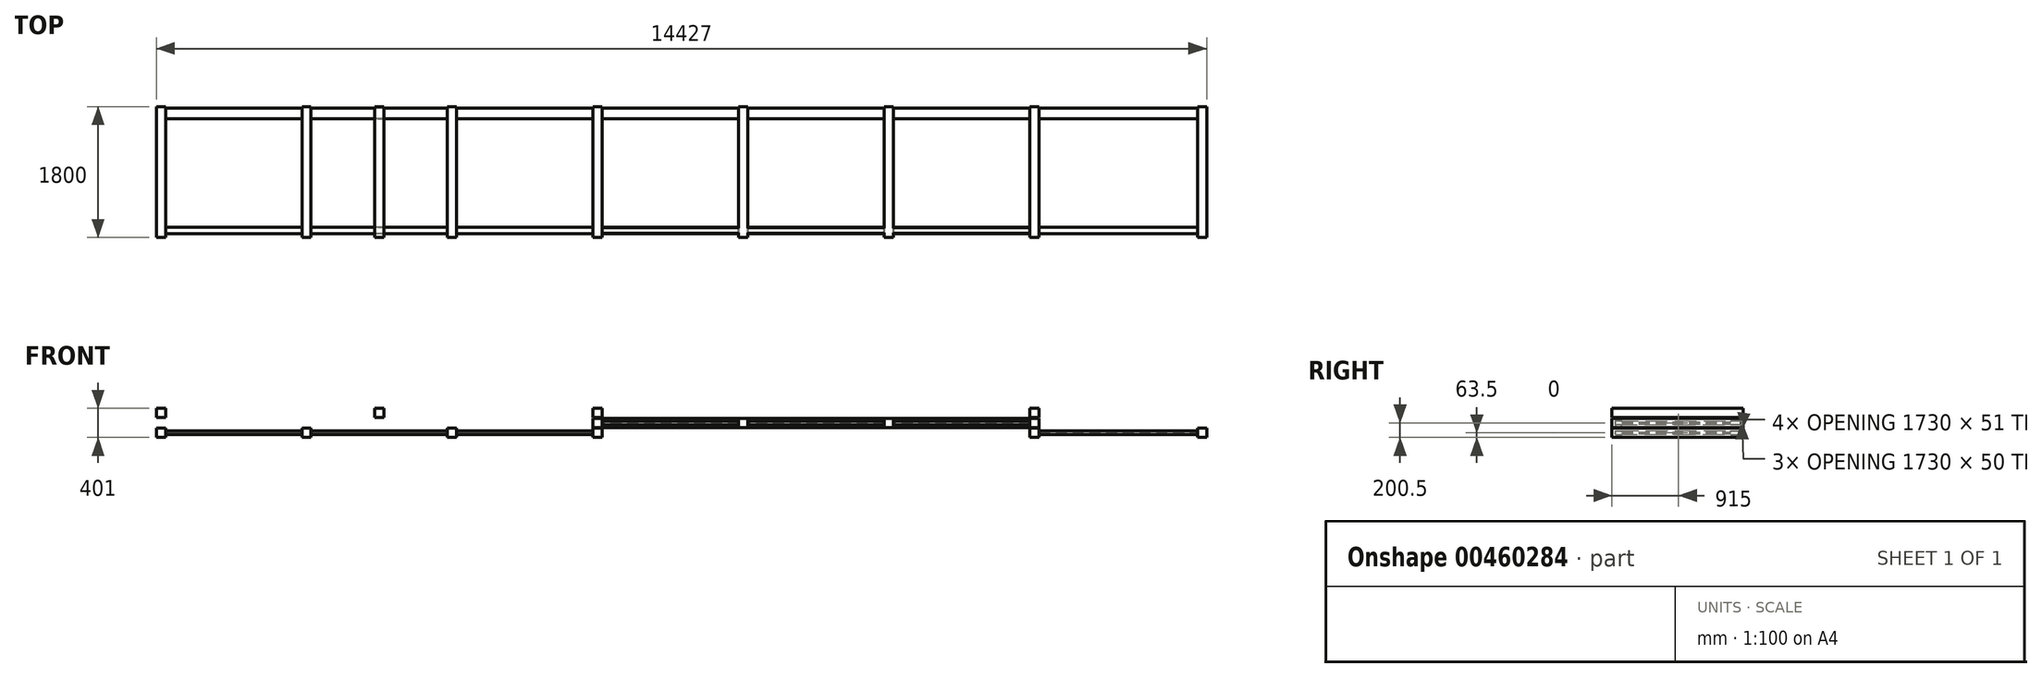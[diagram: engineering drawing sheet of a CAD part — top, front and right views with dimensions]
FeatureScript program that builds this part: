
annotation { "Feature Type Name" : "Feature", "Feature Type Description" : "" }
export const myFeature = defineFeature(function(context is Context, id is Id, definition is map)
    precondition{}
    {
        {
            var Q0;
            Q0=qCreatedBy(makeId("Front.planeOp"),FACE);
            var sketch = newSketch(context, id + "F0", { "sketchPlane" : qUnion([Q0])});
            skLineSegment(sketch, "E0.bottom", {"start": v(2923.43, -12.5) * mm, "end": v(-3076.57, -12.5) * mm});
            skLineSegment(sketch, "E0.top", {"start": v(2923.43, 12.5) * mm, "end": v(-3076.57, 12.5) * mm});
            skLineSegment(sketch, "E0.left", {"start": v(2923.43, -12.5) * mm, "end": v(2923.43, 12.5) * mm});
            skLineSegment(sketch, "E0.right", {"start": v(-3076.57, -12.5) * mm, "end": v(-3076.57, 12.5) * mm});
            skPoint(sketch, "E0.middle", {"position": v(-1076.57, 0) * mm});
            skLineSegment(sketch, "E1.bottom", {"start": v(2986.93, -63.5) * mm, "end": v(2859.93, -63.5) * mm});
            skLineSegment(sketch, "E1.top", {"start": v(2986.93, 63.5) * mm, "end": v(2859.93, 63.5) * mm});
            skLineSegment(sketch, "E1.left", {"start": v(2986.93, -63.5) * mm, "end": v(2986.93, 63.5) * mm});
            skLineSegment(sketch, "E1.right", {"start": v(2859.93, -63.5) * mm, "end": v(2859.93, 63.5) * mm});
            skPoint(sketch, "E1.middle", {"position": v(2923.43, 0) * mm});
            skLineSegment(sketch, "E2.bottom", {"start": v(-3013.07, -63.5) * mm, "end": v(-3140.07, -63.5) * mm});
            skLineSegment(sketch, "E2.top", {"start": v(-3013.07, 63.5) * mm, "end": v(-3140.07, 63.5) * mm});
            skLineSegment(sketch, "E2.left", {"start": v(-3013.07, -63.5) * mm, "end": v(-3013.07, 63.5) * mm});
            skLineSegment(sketch, "E2.right", {"start": v(-3140.07, -63.5) * mm, "end": v(-3140.07, 63.5) * mm});
            skPoint(sketch, "E2.middle", {"position": v(-3076.57, 0) * mm});
            skLineSegment(sketch, "E3.bottom", {"start": v(-1013.07, -63.5) * mm, "end": v(-1140.07, -63.5) * mm});
            skLineSegment(sketch, "E3.top", {"start": v(-1013.07, 63.5) * mm, "end": v(-1140.07, 63.5) * mm});
            skLineSegment(sketch, "E3.left", {"start": v(-1013.07, -63.5) * mm, "end": v(-1013.07, 63.5) * mm});
            skLineSegment(sketch, "E3.right", {"start": v(-1140.07, -63.5) * mm, "end": v(-1140.07, 63.5) * mm});
            skPoint(sketch, "E4.middle", {"position": v(923.43, 0) * mm});
            skLineSegment(sketch, "E5.bottom", {"start": v(986.93, -63.5) * mm, "end": v(859.93, -63.5) * mm});
            skLineSegment(sketch, "E5.top", {"start": v(986.93, 63.5) * mm, "end": v(859.93, 63.5) * mm});
            skLineSegment(sketch, "E5.left", {"start": v(986.93, -63.5) * mm, "end": v(986.93, 63.5) * mm});
            skLineSegment(sketch, "E5.right", {"start": v(859.93, -63.5) * mm, "end": v(859.93, 63.5) * mm});
            skLineSegment(sketch, "E6.bottom", {"start": v(-3013.07, -200.5) * mm, "end": v(-3140.07, -200.5) * mm});
            skLineSegment(sketch, "E6.top", {"start": v(-3013.07, -73.5) * mm, "end": v(-3140.07, -73.5) * mm});
            skLineSegment(sketch, "E6.left", {"start": v(-3013.07, -200.5) * mm, "end": v(-3013.07, -73.5) * mm});
            skLineSegment(sketch, "E6.right", {"start": v(-3140.07, -200.5) * mm, "end": v(-3140.07, -73.5) * mm});
            skPoint(sketch, "E6.middle", {"position": v(-3076.57, -137) * mm});
            skLineSegment(sketch, "E7.1.0.0", {"start": v(-5013.07, -200.5) * mm, "end": v(-5140.07, -200.5) * mm});
            skLineSegment(sketch, "E7.1.0.1", {"start": v(-5140.07, -200.5) * mm, "end": v(-5140.07, -73.5) * mm});
            skLineSegment(sketch, "E7.1.0.2", {"start": v(-5013.07, -73.5) * mm, "end": v(-5140.07, -73.5) * mm});
            skLineSegment(sketch, "E7.1.0.3", {"start": v(-5013.07, -200.5) * mm, "end": v(-5013.07, -73.5) * mm});
            skLineSegment(sketch, "E7.2.0.0", {"start": v(-7013.07, -200.5) * mm, "end": v(-7140.07, -200.5) * mm});
            skLineSegment(sketch, "E7.2.0.1", {"start": v(-7140.07, -200.5) * mm, "end": v(-7140.07, -73.5) * mm});
            skLineSegment(sketch, "E7.2.0.2", {"start": v(-7013.07, -73.5) * mm, "end": v(-7140.07, -73.5) * mm});
            skLineSegment(sketch, "E7.2.0.3", {"start": v(-7013.07, -200.5) * mm, "end": v(-7013.07, -73.5) * mm});
            skLineSegment(sketch, "E7.3.0.0", {"start": v(-9013.07, -200.5) * mm, "end": v(-9140.07, -200.5) * mm});
            skLineSegment(sketch, "E7.3.0.1", {"start": v(-9140.07, -200.5) * mm, "end": v(-9140.07, -73.5) * mm});
            skLineSegment(sketch, "E7.3.0.2", {"start": v(-9013.07, -73.5) * mm, "end": v(-9140.07, -73.5) * mm});
            skLineSegment(sketch, "E7.3.0.3", {"start": v(-9013.07, -200.5) * mm, "end": v(-9013.07, -73.5) * mm});
            skLineSegment(sketch, "E7.direction1", {"start": v(-3140.07, -200.5) * mm, "end": v(-5140.07, -200.5) * mm, "construction": true});
            skLineSegment(sketch, "E8", {"start": v(-9013.07, -126) * mm, "end": v(-3140.07, -126) * mm});
            skLineSegment(sketch, "E9", {"start": v(-3140.07, -148) * mm, "end": v(-9013.07, -148) * mm});
            skLineSegment(sketch, "E10.bottom", {"start": v(2986.93, -200.5) * mm, "end": v(2859.93, -200.5) * mm});
            skLineSegment(sketch, "E10.top", {"start": v(2986.93, -73.5) * mm, "end": v(2859.93, -73.5) * mm});
            skLineSegment(sketch, "E10.left", {"start": v(2986.93, -200.5) * mm, "end": v(2986.93, -73.5) * mm});
            skLineSegment(sketch, "E10.right", {"start": v(2859.93, -200.5) * mm, "end": v(2859.93, -73.5) * mm});
            skPoint(sketch, "E10.middle", {"position": v(2923.43, -137) * mm});
            skPoint(sketch, "E10.cornerSnap0", {"position": v(2986.93, 0) * mm});
            skLineSegment(sketch, "E11.1.0.0", {"start": v(5286.93, -200.5) * mm, "end": v(5159.93, -200.5) * mm});
            skLineSegment(sketch, "E11.1.0.1", {"start": v(5159.93, -200.5) * mm, "end": v(5159.93, -73.5) * mm});
            skLineSegment(sketch, "E11.1.0.2", {"start": v(5286.93, -73.5) * mm, "end": v(5159.93, -73.5) * mm});
            skLineSegment(sketch, "E11.1.0.3", {"start": v(5286.93, -200.5) * mm, "end": v(5286.93, -73.5) * mm});
            skLineSegment(sketch, "E11.direction1", {"start": v(2859.93, -200.5) * mm, "end": v(5159.93, -200.5) * mm, "construction": true});
            skLineSegment(sketch, "E12", {"start": v(2986.93, -126) * mm, "end": v(5159.93, -126) * mm});
            skLineSegment(sketch, "E13", {"start": v(2986.93, -148) * mm, "end": v(5159.93, -148) * mm});
            skLineSegment(sketch, "E14.bottom", {"start": v(2986.93, 73.5) * mm, "end": v(2859.93, 73.5) * mm});
            skLineSegment(sketch, "E14.top", {"start": v(2986.93, 200.5) * mm, "end": v(2859.93, 200.5) * mm});
            skLineSegment(sketch, "E14.left", {"start": v(2986.93, 73.5) * mm, "end": v(2986.93, 200.5) * mm});
            skLineSegment(sketch, "E14.right", {"start": v(2859.93, 73.5) * mm, "end": v(2859.93, 200.5) * mm});
            skPoint(sketch, "E14.middle", {"position": v(2923.43, 137) * mm});
            skLineSegment(sketch, "E15.bottom", {"start": v(-3013.07, 73.5) * mm, "end": v(-3140.07, 73.5) * mm});
            skLineSegment(sketch, "E15.top", {"start": v(-3013.07, 200.5) * mm, "end": v(-3140.07, 200.5) * mm});
            skLineSegment(sketch, "E15.left", {"start": v(-3013.07, 73.5) * mm, "end": v(-3013.07, 200.5) * mm});
            skLineSegment(sketch, "E15.right", {"start": v(-3140.07, 73.5) * mm, "end": v(-3140.07, 200.5) * mm});
            skPoint(sketch, "E15.middle", {"position": v(-3076.57, 137) * mm});
            skLineSegment(sketch, "E16.bottom", {"start": v(-9140.07, 73.5) * mm, "end": v(-9013.07, 73.5) * mm});
            skLineSegment(sketch, "E16.top", {"start": v(-9140.07, 200.5) * mm, "end": v(-9013.07, 200.5) * mm});
            skLineSegment(sketch, "E16.left", {"start": v(-9140.07, 73.5) * mm, "end": v(-9140.07, 200.5) * mm});
            skLineSegment(sketch, "E16.right", {"start": v(-9013.07, 73.5) * mm, "end": v(-9013.07, 200.5) * mm});
            skLineSegment(sketch, "E17.bottom", {"start": v(-6140.07, 73.5) * mm, "end": v(-6013.07, 73.5) * mm});
            skLineSegment(sketch, "E17.top", {"start": v(-6140.07, 200.5) * mm, "end": v(-6013.07, 200.5) * mm});
            skLineSegment(sketch, "E17.left", {"start": v(-6140.07, 73.5) * mm, "end": v(-6140.07, 200.5) * mm});
            skLineSegment(sketch, "E17.right", {"start": v(-6013.07, 73.5) * mm, "end": v(-6013.07, 200.5) * mm});
            skSolve(sketch);
        }
        {
            var Q0;
            {var subQ0=sQuery(id+"F0.wireOp",EDGE,"E3.right");var subQ1=sQuery(id+"F0.wireOp",EDGE,"E0.bottom");var subQ2=makeQuery(id+"F0.imprint","INTERSECT",VERTEX,{"derivedFrom":[subQ1,subQ0]});Q0=makeQuery(id+"F0.imprint","IMPRINT",FACE,{"disambiguationData":[TD([[makeQuery(id+"F0.imprint","IMPRINT",EDGE,{"disambiguationData":[TD([[subQ2,-1.0]])],"derivedFrom":subQ1}),-1.0]])]});}
            var Q1;
            {var subQ0=sQuery(id+"F0.wireOp",EDGE,"E0.right");Q1=makeQuery(id+"F0.imprint","IMPRINT",FACE,{"disambiguationData":[TD([[makeQuery(id+"F0.imprint","IMPRINT",EDGE,{"derivedFrom":subQ0}),-1.0]])]});}
            var Q2;
            {var subQ0=sQuery(id+"F0.wireOp",EDGE,"E3.left");var subQ1=sQuery(id+"F0.wireOp",EDGE,"E0.bottom");var subQ2=makeQuery(id+"F0.imprint","INTERSECT",VERTEX,{"derivedFrom":[subQ1,subQ0]});Q2=makeQuery(id+"F0.imprint","IMPRINT",FACE,{"disambiguationData":[TD([[makeQuery(id+"F0.imprint","IMPRINT",EDGE,{"disambiguationData":[TD([[subQ2,-1.0]])],"derivedFrom":subQ1}),-1.0]])]});}
            var Q3;
            {var subQ0=sQuery(id+"F0.wireOp",EDGE,"E5.right");var subQ1=sQuery(id+"F0.wireOp",EDGE,"E0.bottom");var subQ2=makeQuery(id+"F0.imprint","INTERSECT",VERTEX,{"derivedFrom":[subQ1,subQ0]});Q3=makeQuery(id+"F0.imprint","IMPRINT",FACE,{"disambiguationData":[TD([[makeQuery(id+"F0.imprint","IMPRINT",EDGE,{"disambiguationData":[TD([[subQ2,-1.0]])],"derivedFrom":subQ1}),-1.0]])]});}
            var Q4;
            {var subQ0=sQuery(id+"F0.wireOp",EDGE,"E5.left");var subQ1=sQuery(id+"F0.wireOp",EDGE,"E0.bottom");var subQ2=makeQuery(id+"F0.imprint","INTERSECT",VERTEX,{"derivedFrom":[subQ1,subQ0]});Q4=makeQuery(id+"F0.imprint","IMPRINT",FACE,{"disambiguationData":[TD([[makeQuery(id+"F0.imprint","IMPRINT",EDGE,{"disambiguationData":[TD([[subQ2,-1.0]])],"derivedFrom":subQ1}),-1.0]])]});}
            var Q5;
            {var subQ0=sQuery(id+"F0.wireOp",EDGE,"E1.right");var subQ1=sQuery(id+"F0.wireOp",EDGE,"E0.bottom");var subQ2=makeQuery(id+"F0.imprint","INTERSECT",VERTEX,{"derivedFrom":[subQ1,subQ0]});Q5=makeQuery(id+"F0.imprint","IMPRINT",FACE,{"disambiguationData":[TD([[makeQuery(id+"F0.imprint","IMPRINT",EDGE,{"disambiguationData":[TD([[subQ2,-1.0]])],"derivedFrom":subQ1}),-1.0]])]});}
            var Q6;
            {var subQ0=sQuery(id+"F0.wireOp",EDGE,"E0.left");Q6=makeQuery(id+"F0.imprint","IMPRINT",FACE,{"disambiguationData":[TD([[makeQuery(id+"F0.imprint","IMPRINT",EDGE,{"derivedFrom":subQ0}),1.0]])]});}
            var Q7;
            {var subQ1=sQuery(id+"F0.wireOp",EDGE,"E0.right");Q7=makeQuery(id+"F0.imprint","IMPRINT",FACE,{"disambiguationData":[TD([[makeQuery(id+"F0.imprint","IMPRINT",EDGE,{"derivedFrom":subQ1}),1.0]])]});}
            var Q8;
            {var subQ5=sQuery(id+"F0.wireOp",EDGE,"E3.bottom");Q8=makeQuery(id+"F0.imprint","IMPRINT",FACE,{"disambiguationData":[TD([[makeQuery(id+"F0.imprint","IMPRINT",EDGE,{"derivedFrom":subQ5}),-1.0]])]});}
            var Q9;
            {var subQ5=sQuery(id+"F0.wireOp",EDGE,"E3.top");Q9=makeQuery(id+"F0.imprint","IMPRINT",FACE,{"disambiguationData":[TD([[makeQuery(id+"F0.imprint","IMPRINT",EDGE,{"derivedFrom":subQ5}),1.0]])]});}
            var Q10;
            {var subQ5=sQuery(id+"F0.wireOp",EDGE,"E5.bottom");Q10=makeQuery(id+"F0.imprint","IMPRINT",FACE,{"disambiguationData":[TD([[makeQuery(id+"F0.imprint","IMPRINT",EDGE,{"derivedFrom":subQ5}),-1.0]])]});}
            var Q11;
            {var subQ5=sQuery(id+"F0.wireOp",EDGE,"E5.top");Q11=makeQuery(id+"F0.imprint","IMPRINT",FACE,{"disambiguationData":[TD([[makeQuery(id+"F0.imprint","IMPRINT",EDGE,{"derivedFrom":subQ5}),1.0]])]});}
            var Q12;
            {var subQ1=sQuery(id+"F0.wireOp",EDGE,"E0.left");Q12=makeQuery(id+"F0.imprint","IMPRINT",FACE,{"disambiguationData":[TD([[makeQuery(id+"F0.imprint","IMPRINT",EDGE,{"derivedFrom":subQ1}),-1.0]])]});}
            extrude(context, id + "F1", {"entities" : qUnion([Q0, Q1, Q2, Q3, Q4, Q5, Q6, Q7, Q8, Q9, Q10, Q11, Q12]), "depth" : 1800 * mm});
        }
        {
            var Q0;
            Q0=makeQuery(id+"F1.opExtrude","SWEPT_FACE",FACE,{"disambiguationData":[OSD([sQuery(id+"F0.wireOp",EDGE,"E2.right")])]});
            var sketch = newSketch(context, id + "F2", { "sketchPlane" : qUnion([Q0])});
            skLineSegment(sketch, "E18.bottom", {"start": v(20, -25) * mm, "end": v(170, -25) * mm});
            skLineSegment(sketch, "E18.top", {"start": v(20, 25) * mm, "end": v(170, 25) * mm});
            skLineSegment(sketch, "E18.left", {"start": v(20, -25) * mm, "end": v(20, 25) * mm});
            skLineSegment(sketch, "E18.right", {"start": v(170, -25) * mm, "end": v(170, 25) * mm});
            skPoint(sketch, "E18.middle", {"position": v(95, 0) * mm});
            skLineSegment(sketch, "E19.bottom", {"start": v(1662, -25) * mm, "end": v(1750, -25) * mm});
            skLineSegment(sketch, "E19.top", {"start": v(1662, 25) * mm, "end": v(1750, 25) * mm});
            skLineSegment(sketch, "E19.left", {"start": v(1662, -25) * mm, "end": v(1662, 25) * mm});
            skLineSegment(sketch, "E19.right", {"start": v(1750, -25) * mm, "end": v(1750, 25) * mm});
            skPoint(sketch, "E19.middle", {"position": v(1706, 0) * mm});
            skPoint(sketch, "E20.startSnap0", {"position": v(1800, 0) * mm});
            skPoint(sketch, "E20.endSnap0", {"position": v(1800, 0) * mm});
            skSolve(sketch);
        }
        {
            var Q0;
            Q0 = qSketchRegion(id + "F2", true);
            extrude(context, id + "F3", {"entities" : qUnion([Q0]), "operationType" : NewBodyOperationType.ADD, "oppositeDirection" : true, "depth" : 6000 * mm});
        }
        {
            var Q0;
            {var subQ2=sQuery(id+"F0.wireOp",EDGE,"E1.right");var subQ4=sQuery(id+"F0.wireOp",EDGE,"E0.top");var subQ5=makeQuery(id+"F0.imprint","INTERSECT",VERTEX,{"derivedFrom":[subQ4,subQ2]});Q0=makeQuery(id+"F3.boolean.opBoolean","SPLIT",FACE,{"disambiguationData":[TD([makeQuery(id+"F3.opExtrude","SWEPT_FACE",FACE,{"disambiguationData":[OSD([sQuery(id+"F2.wireOp",EDGE,"E19.right")])]})])],"derivedFrom":makeQuery(id+"F1.opExtrude","SWEPT_FACE",FACE,{"disambiguationData":[OSD([subQ4]),TDD([makeQuery(id+"F0.imprint","IMPRINT",EDGE,{"disambiguationData":[TD([[subQ5,-1.0]])],"derivedFrom":subQ4})])]})});}
            var Q1;
            {var subQ0=sQuery(id+"F0.wireOp",EDGE,"E5.right");var subQ4=sQuery(id+"F0.wireOp",EDGE,"E0.top");var subQ6=makeQuery(id+"F0.imprint","INTERSECT",VERTEX,{"derivedFrom":[subQ4,subQ0]});Q1=makeQuery(id+"F3.boolean.opBoolean","SPLIT",FACE,{"disambiguationData":[TD([makeQuery(id+"F3.opExtrude","SWEPT_FACE",FACE,{"disambiguationData":[OSD([sQuery(id+"F2.wireOp",EDGE,"E19.right")])]})])],"derivedFrom":makeQuery(id+"F1.opExtrude","SWEPT_FACE",FACE,{"disambiguationData":[OSD([subQ4]),TDD([makeQuery(id+"F0.imprint","IMPRINT",EDGE,{"disambiguationData":[TD([[subQ6,-1.0]])],"derivedFrom":subQ4})])]})});}
            var Q2;
            {var subQ0=sQuery(id+"F0.wireOp",EDGE,"E3.right");var subQ4=sQuery(id+"F0.wireOp",EDGE,"E0.top");var subQ6=makeQuery(id+"F0.imprint","INTERSECT",VERTEX,{"derivedFrom":[subQ4,subQ0]});Q2=makeQuery(id+"F3.boolean.opBoolean","SPLIT",FACE,{"disambiguationData":[TD([makeQuery(id+"F3.opExtrude","SWEPT_FACE",FACE,{"disambiguationData":[OSD([sQuery(id+"F2.wireOp",EDGE,"E19.right")])]})])],"derivedFrom":makeQuery(id+"F1.opExtrude","SWEPT_FACE",FACE,{"disambiguationData":[OSD([subQ4]),TDD([makeQuery(id+"F0.imprint","IMPRINT",EDGE,{"disambiguationData":[TD([[subQ6,-1.0]])],"derivedFrom":subQ4})])]})});}
            var Q3;
            {var subQ0=sQuery(id+"F0.wireOp",EDGE,"E3.right");var subQ4=sQuery(id+"F0.wireOp",EDGE,"E0.top");var subQ6=makeQuery(id+"F0.imprint","INTERSECT",VERTEX,{"derivedFrom":[subQ4,subQ0]});Q3=makeQuery(id+"F3.boolean.opBoolean","SPLIT",FACE,{"disambiguationData":[TD([makeQuery(id+"F3.opExtrude","SWEPT_FACE",FACE,{"disambiguationData":[OSD([sQuery(id+"F2.wireOp",EDGE,"E18.left")])]})])],"derivedFrom":makeQuery(id+"F1.opExtrude","SWEPT_FACE",FACE,{"disambiguationData":[OSD([subQ4]),TDD([makeQuery(id+"F0.imprint","IMPRINT",EDGE,{"disambiguationData":[TD([[subQ6,-1.0]])],"derivedFrom":subQ4})])]})});}
            var Q4;
            {var subQ0=sQuery(id+"F0.wireOp",EDGE,"E5.right");var subQ4=sQuery(id+"F0.wireOp",EDGE,"E0.top");var subQ6=makeQuery(id+"F0.imprint","INTERSECT",VERTEX,{"derivedFrom":[subQ4,subQ0]});Q4=makeQuery(id+"F3.boolean.opBoolean","SPLIT",FACE,{"disambiguationData":[TD([makeQuery(id+"F3.opExtrude","SWEPT_FACE",FACE,{"disambiguationData":[OSD([sQuery(id+"F2.wireOp",EDGE,"E18.left")])]})])],"derivedFrom":makeQuery(id+"F1.opExtrude","SWEPT_FACE",FACE,{"disambiguationData":[OSD([subQ4]),TDD([makeQuery(id+"F0.imprint","IMPRINT",EDGE,{"disambiguationData":[TD([[subQ6,-1.0]])],"derivedFrom":subQ4})])]})});}
            var Q5;
            {var subQ2=sQuery(id+"F0.wireOp",EDGE,"E1.right");var subQ4=sQuery(id+"F0.wireOp",EDGE,"E0.top");var subQ5=makeQuery(id+"F0.imprint","INTERSECT",VERTEX,{"derivedFrom":[subQ4,subQ2]});Q5=makeQuery(id+"F3.boolean.opBoolean","SPLIT",FACE,{"disambiguationData":[TD([makeQuery(id+"F3.opExtrude","SWEPT_FACE",FACE,{"disambiguationData":[OSD([sQuery(id+"F2.wireOp",EDGE,"E18.left")])]})])],"derivedFrom":makeQuery(id+"F1.opExtrude","SWEPT_FACE",FACE,{"disambiguationData":[OSD([subQ4]),TDD([makeQuery(id+"F0.imprint","IMPRINT",EDGE,{"disambiguationData":[TD([[subQ5,-1.0]])],"derivedFrom":subQ4})])]})});}
            extrude(context, id + "F4", {"entities" : qUnion([Q0, Q1, Q2, Q3, Q4, Q5]), "operationType" : NewBodyOperationType.REMOVE, "oppositeDirection" : true, "depth" : 50 * mm});
        }
        {
            var Q0;
            Q0=makeQuery(id+"F0.imprint","IMPRINT",FACE,{"disambiguationData":[TD([[makeQuery(id+"F0.imprint","IMPRINT",EDGE,{"derivedFrom":sQuery(id+"F0.wireOp",EDGE,"E15.bottom")}),-1.0]])]});
            var Q1;
            {var subQ1=sQuery(id+"F0.wireOp",EDGE,"E6.bottom");Q1=makeQuery(id+"F0.imprint","IMPRINT",FACE,{"disambiguationData":[TD([[makeQuery(id+"F0.imprint","IMPRINT",EDGE,{"derivedFrom":subQ1}),-1.0]])]});}
            var Q2;
            {var subQ0=sQuery(id+"F0.wireOp",EDGE,"E8");var subQ1=sQuery(id+"F0.wireOp",EDGE,"E6.right");var subQ2=makeQuery(id+"F0.imprint","INTERSECT",VERTEX,{"derivedFrom":[subQ1,subQ0]});Q2=makeQuery(id+"F0.imprint","IMPRINT",FACE,{"disambiguationData":[TD([[makeQuery(id+"F0.imprint","IMPRINT",EDGE,{"disambiguationData":[TD([[subQ2,1.0]])],"derivedFrom":subQ1}),1.0]])]});}
            var Q3;
            {var subQ0=sQuery(id+"F0.wireOp",EDGE,"E7.1.0.0");Q3=makeQuery(id+"F0.imprint","IMPRINT",FACE,{"disambiguationData":[TD([[makeQuery(id+"F0.imprint","IMPRINT",EDGE,{"derivedFrom":subQ0}),-1.0]])]});}
            var Q4;
            {var subQ0=sQuery(id+"F0.wireOp",EDGE,"E9");var subQ1=sQuery(id+"F0.wireOp",EDGE,"E7.1.0.1");var subQ2=makeQuery(id+"F0.imprint","INTERSECT",VERTEX,{"derivedFrom":[subQ1,subQ0]});Q4=makeQuery(id+"F0.imprint","IMPRINT",FACE,{"disambiguationData":[TD([[makeQuery(id+"F0.imprint","IMPRINT",EDGE,{"disambiguationData":[TD([[subQ2,-1.0]])],"derivedFrom":subQ1}),-1.0]])]});}
            var Q5;
            {var subQ0=sQuery(id+"F0.wireOp",EDGE,"E7.1.0.2");Q5=makeQuery(id+"F0.imprint","IMPRINT",FACE,{"disambiguationData":[TD([[makeQuery(id+"F0.imprint","IMPRINT",EDGE,{"derivedFrom":subQ0}),1.0]])]});}
            var Q6;
            {var subQ0=sQuery(id+"F0.wireOp",EDGE,"E9");var subQ1=sQuery(id+"F0.wireOp",EDGE,"E7.1.0.1");var subQ2=makeQuery(id+"F0.imprint","INTERSECT",VERTEX,{"derivedFrom":[subQ1,subQ0]});Q6=makeQuery(id+"F0.imprint","IMPRINT",FACE,{"disambiguationData":[TD([[makeQuery(id+"F0.imprint","IMPRINT",EDGE,{"disambiguationData":[TD([[subQ2,-1.0]])],"derivedFrom":subQ1}),1.0]])]});}
            var Q7;
            {var subQ0=sQuery(id+"F0.wireOp",EDGE,"E7.2.0.0");Q7=makeQuery(id+"F0.imprint","IMPRINT",FACE,{"disambiguationData":[TD([[makeQuery(id+"F0.imprint","IMPRINT",EDGE,{"derivedFrom":subQ0}),-1.0]])]});}
            var Q8;
            {var subQ0=sQuery(id+"F0.wireOp",EDGE,"E9");var subQ1=sQuery(id+"F0.wireOp",EDGE,"E7.2.0.1");var subQ2=makeQuery(id+"F0.imprint","INTERSECT",VERTEX,{"derivedFrom":[subQ1,subQ0]});Q8=makeQuery(id+"F0.imprint","IMPRINT",FACE,{"disambiguationData":[TD([[makeQuery(id+"F0.imprint","IMPRINT",EDGE,{"disambiguationData":[TD([[subQ2,-1.0]])],"derivedFrom":subQ1}),-1.0]])]});}
            var Q9;
            {var subQ0=sQuery(id+"F0.wireOp",EDGE,"E7.2.0.2");Q9=makeQuery(id+"F0.imprint","IMPRINT",FACE,{"disambiguationData":[TD([[makeQuery(id+"F0.imprint","IMPRINT",EDGE,{"derivedFrom":subQ0}),1.0]])]});}
            var Q10;
            Q10=makeQuery(id+"F0.imprint","IMPRINT",FACE,{"disambiguationData":[TD([[makeQuery(id+"F0.imprint","IMPRINT",EDGE,{"derivedFrom":sQuery(id+"F0.wireOp",EDGE,"E17.bottom")}),1.0]])]});
            var Q11;
            {var subQ0=sQuery(id+"F0.wireOp",EDGE,"E9");var subQ1=sQuery(id+"F0.wireOp",EDGE,"E7.2.0.1");var subQ2=makeQuery(id+"F0.imprint","INTERSECT",VERTEX,{"derivedFrom":[subQ1,subQ0]});Q11=makeQuery(id+"F0.imprint","IMPRINT",FACE,{"disambiguationData":[TD([[makeQuery(id+"F0.imprint","IMPRINT",EDGE,{"disambiguationData":[TD([[subQ2,-1.0]])],"derivedFrom":subQ1}),1.0]])]});}
            var Q12;
            {var subQ1=sQuery(id+"F0.wireOp",EDGE,"E7.3.0.0");Q12=makeQuery(id+"F0.imprint","IMPRINT",FACE,{"disambiguationData":[TD([[makeQuery(id+"F0.imprint","IMPRINT",EDGE,{"derivedFrom":subQ1}),-1.0]])]});}
            var Q13;
            Q13=makeQuery(id+"F0.imprint","IMPRINT",FACE,{"disambiguationData":[TD([[makeQuery(id+"F0.imprint","IMPRINT",EDGE,{"derivedFrom":sQuery(id+"F0.wireOp",EDGE,"E16.bottom")}),1.0]])]});
            var Q14;
            {var subQ3=sQuery(id+"F0.wireOp",EDGE,"E10.bottom");Q14=makeQuery(id+"F0.imprint","IMPRINT",FACE,{"disambiguationData":[TD([[makeQuery(id+"F0.imprint","IMPRINT",EDGE,{"derivedFrom":subQ3}),-1.0]])]});}
            var Q15;
            Q15=makeQuery(id+"F0.imprint","IMPRINT",FACE,{"disambiguationData":[TD([[makeQuery(id+"F0.imprint","IMPRINT",EDGE,{"derivedFrom":sQuery(id+"F0.wireOp",EDGE,"E14.bottom")}),-1.0]])]});
            var Q16;
            {var subQ0=sQuery(id+"F0.wireOp",EDGE,"E12");Q16=makeQuery(id+"F0.imprint","IMPRINT",FACE,{"disambiguationData":[TD([[makeQuery(id+"F0.imprint","IMPRINT",EDGE,{"derivedFrom":subQ0}),-1.0]])]});}
            var Q17;
            {var subQ4=sQuery(id+"F0.wireOp",EDGE,"E11.1.0.0");Q17=makeQuery(id+"F0.imprint","IMPRINT",FACE,{"disambiguationData":[TD([[makeQuery(id+"F0.imprint","IMPRINT",EDGE,{"derivedFrom":subQ4}),-1.0]])]});}
            extrude(context, id + "F5", {"entities" : qUnion([Q0, Q1, Q2, Q3, Q4, Q5, Q6, Q7, Q8, Q9, Q10, Q11, Q12, Q13, Q14, Q15, Q16, Q17]), "depth" : 1800 * mm});
        }
        {
            var Q0;
            Q0=makeQuery(id+"F5.opExtrude","SWEPT_FACE",FACE,{"disambiguationData":[OSD([sQuery(id+"F0.wireOp",EDGE,"E11.1.0.3")])]});
            var sketch = newSketch(context, id + "F6", { "sketchPlane" : qUnion([Q0])});
            skLineSegment(sketch, "E21.bottom", {"start": v(-20, -111.5) * mm, "end": v(-170, -111.5) * mm});
            skLineSegment(sketch, "E21.top", {"start": v(-20, -162.5) * mm, "end": v(-170, -162.5) * mm});
            skLineSegment(sketch, "E21.left", {"start": v(-20, -111.5) * mm, "end": v(-20, -162.5) * mm});
            skLineSegment(sketch, "E21.right", {"start": v(-170, -111.5) * mm, "end": v(-170, -162.5) * mm});
            skPoint(sketch, "E21.middle", {"position": v(-95, -137) * mm});
            skPoint(sketch, "E21.middle.positionSnap0", {"position": v(0, -137) * mm});
            skPoint(sketch, "E21.centerSnap0", {"position": v(0, -137) * mm});
            skLineSegment(sketch, "E22.bottom", {"start": v(-1662, -111.5) * mm, "end": v(-1750, -111.5) * mm});
            skLineSegment(sketch, "E22.top", {"start": v(-1662, -162.5) * mm, "end": v(-1750, -162.5) * mm});
            skLineSegment(sketch, "E22.left", {"start": v(-1662, -111.5) * mm, "end": v(-1662, -162.5) * mm});
            skLineSegment(sketch, "E22.right", {"start": v(-1750, -111.5) * mm, "end": v(-1750, -162.5) * mm});
            skPoint(sketch, "E22.middle", {"position": v(-1706, -137) * mm});
            skPoint(sketch, "E22.middle.positionSnap0", {"position": v(-1800, -137) * mm});
            skPoint(sketch, "E22.centerSnap0", {"position": v(-1800, -137) * mm});
            skSolve(sketch);
        }
        {
            var Q0;
            Q0 = qSketchRegion(id + "F6", true);
            extrude(context, id + "F7", {"entities" : qUnion([Q0]), "operationType" : NewBodyOperationType.ADD, "oppositeDirection" : true, "depth" : 2370 * mm});
        }
        {
            var Q0;
            Q0=makeQuery(id+"F5.opExtrude","SWEPT_FACE",FACE,{"disambiguationData":[OSD([sQuery(id+"F0.wireOp",EDGE,"E7.3.0.1")])]});
            var sketch = newSketch(context, id + "F8", { "sketchPlane" : qUnion([Q0])});
            skLineSegment(sketch, "E23.bottom", {"start": v(20, -162.5) * mm, "end": v(170, -162.5) * mm});
            skLineSegment(sketch, "E23.top", {"start": v(20, -111.5) * mm, "end": v(170, -111.5) * mm});
            skLineSegment(sketch, "E23.left", {"start": v(20, -162.5) * mm, "end": v(20, -111.5) * mm});
            skLineSegment(sketch, "E23.right", {"start": v(170, -162.5) * mm, "end": v(170, -111.5) * mm});
            skPoint(sketch, "E23.middle", {"position": v(95, -137) * mm});
            skPoint(sketch, "E23.middle.positionSnap0", {"position": v(0, -137) * mm});
            skPoint(sketch, "E23.centerSnap0", {"position": v(0, -137) * mm});
            skLineSegment(sketch, "E24.bottom", {"start": v(1662, -162.5) * mm, "end": v(1750, -162.5) * mm});
            skLineSegment(sketch, "E24.top", {"start": v(1662, -111.5) * mm, "end": v(1750, -111.5) * mm});
            skLineSegment(sketch, "E24.left", {"start": v(1662, -162.5) * mm, "end": v(1662, -111.5) * mm});
            skLineSegment(sketch, "E24.right", {"start": v(1750, -162.5) * mm, "end": v(1750, -111.5) * mm});
            skPoint(sketch, "E24.middle", {"position": v(1706, -137) * mm});
            skPoint(sketch, "E24.middle.positionSnap0", {"position": v(1800, -137) * mm});
            skPoint(sketch, "E24.centerSnap0", {"position": v(1800, -137) * mm});
            skSolve(sketch);
        }
        {
            var Q0;
            Q0 = qSketchRegion(id + "F8", true);
            extrude(context, id + "F9", {"entities" : qUnion([Q0]), "operationType" : NewBodyOperationType.ADD, "oppositeDirection" : true, "depth" : 6090 * mm});
        }
        {
            var Q0;
            {var subQ0=sQuery(id+"F0.wireOp",EDGE,"E13");Q0=makeQuery(id+"F7.boolean.opBoolean","SPLIT",FACE,{"disambiguationData":[TD([makeQuery(id+"F7.opExtrude","SWEPT_FACE",FACE,{"disambiguationData":[OSD([sQuery(id+"F6.wireOp",EDGE,"E22.right")])]})])],"derivedFrom":makeQuery(id+"F5.opExtrude","SWEPT_FACE",FACE,{"disambiguationData":[OSD([subQ0])]})});}
            var Q1;
            {var subQ0=sQuery(id+"F0.wireOp",EDGE,"E13");Q1=makeQuery(id+"F7.boolean.opBoolean","SPLIT",FACE,{"disambiguationData":[TD([makeQuery(id+"F7.opExtrude","SWEPT_FACE",FACE,{"disambiguationData":[OSD([sQuery(id+"F6.wireOp",EDGE,"E21.left")])]})])],"derivedFrom":makeQuery(id+"F5.opExtrude","SWEPT_FACE",FACE,{"disambiguationData":[OSD([subQ0])]})});}
            var Q2;
            {var subQ0=sQuery(id+"F0.wireOp",EDGE,"E9");var subQ3=sQuery(id+"F0.wireOp",EDGE,"E6.right");var subQ5=makeQuery(id+"F0.imprint","INTERSECT",VERTEX,{"derivedFrom":[subQ3,subQ0]});Q2=makeQuery(id+"F9.boolean.opBoolean","SPLIT",FACE,{"disambiguationData":[TD([makeQuery(id+"F9.opExtrude","SWEPT_FACE",FACE,{"disambiguationData":[OSD([sQuery(id+"F8.wireOp",EDGE,"E24.right")])]})])],"derivedFrom":makeQuery(id+"F5.opExtrude","SWEPT_FACE",FACE,{"disambiguationData":[OSD([subQ0]),TDD([makeQuery(id+"F0.imprint","IMPRINT",EDGE,{"disambiguationData":[TD([[subQ5,-1.0]])],"derivedFrom":subQ0})])]})});}
            var Q3;
            {var subQ0=sQuery(id+"F0.wireOp",EDGE,"E9");var subQ3=sQuery(id+"F0.wireOp",EDGE,"E7.1.0.1");var subQ6=makeQuery(id+"F0.imprint","INTERSECT",VERTEX,{"derivedFrom":[subQ3,subQ0]});Q3=makeQuery(id+"F9.boolean.opBoolean","SPLIT",FACE,{"disambiguationData":[TD([makeQuery(id+"F9.opExtrude","SWEPT_FACE",FACE,{"disambiguationData":[OSD([sQuery(id+"F8.wireOp",EDGE,"E24.right")])]})])],"derivedFrom":makeQuery(id+"F5.opExtrude","SWEPT_FACE",FACE,{"disambiguationData":[OSD([subQ0]),TDD([makeQuery(id+"F0.imprint","IMPRINT",EDGE,{"disambiguationData":[TD([[subQ6,-1.0]])],"derivedFrom":subQ0})])]})});}
            var Q4;
            {var subQ0=sQuery(id+"F0.wireOp",EDGE,"E9");var subQ1=sQuery(id+"F0.wireOp",EDGE,"E7.3.0.3");var subQ5=makeQuery(id+"F0.imprint","INTERSECT",VERTEX,{"derivedFrom":[subQ1,subQ0]});Q4=makeQuery(id+"F9.boolean.opBoolean","SPLIT",FACE,{"disambiguationData":[TD([makeQuery(id+"F9.opExtrude","SWEPT_FACE",FACE,{"disambiguationData":[OSD([sQuery(id+"F8.wireOp",EDGE,"E24.right")])]})])],"derivedFrom":makeQuery(id+"F5.opExtrude","SWEPT_FACE",FACE,{"disambiguationData":[OSD([subQ0]),TDD([makeQuery(id+"F0.imprint","IMPRINT",EDGE,{"disambiguationData":[TD([[subQ5,1.0]])],"derivedFrom":subQ0})])]})});}
            var Q5;
            {var subQ0=sQuery(id+"F0.wireOp",EDGE,"E9");var subQ1=sQuery(id+"F0.wireOp",EDGE,"E7.3.0.3");var subQ6=makeQuery(id+"F0.imprint","INTERSECT",VERTEX,{"derivedFrom":[subQ1,subQ0]});Q5=makeQuery(id+"F9.boolean.opBoolean","SPLIT",FACE,{"disambiguationData":[TD([makeQuery(id+"F9.opExtrude","SWEPT_FACE",FACE,{"disambiguationData":[OSD([sQuery(id+"F8.wireOp",EDGE,"E23.left")])]})])],"derivedFrom":makeQuery(id+"F5.opExtrude","SWEPT_FACE",FACE,{"disambiguationData":[OSD([subQ0]),TDD([makeQuery(id+"F0.imprint","IMPRINT",EDGE,{"disambiguationData":[TD([[subQ6,1.0]])],"derivedFrom":subQ0})])]})});}
            var Q6;
            {var subQ0=sQuery(id+"F0.wireOp",EDGE,"E9");var subQ3=sQuery(id+"F0.wireOp",EDGE,"E7.1.0.1");var subQ5=makeQuery(id+"F0.imprint","INTERSECT",VERTEX,{"derivedFrom":[subQ3,subQ0]});Q6=makeQuery(id+"F9.boolean.opBoolean","SPLIT",FACE,{"disambiguationData":[TD([makeQuery(id+"F9.opExtrude","SWEPT_FACE",FACE,{"disambiguationData":[OSD([sQuery(id+"F8.wireOp",EDGE,"E23.left")])]})])],"derivedFrom":makeQuery(id+"F5.opExtrude","SWEPT_FACE",FACE,{"disambiguationData":[OSD([subQ0]),TDD([makeQuery(id+"F0.imprint","IMPRINT",EDGE,{"disambiguationData":[TD([[subQ5,-1.0]])],"derivedFrom":subQ0})])]})});}
            var Q7;
            {var subQ0=sQuery(id+"F0.wireOp",EDGE,"E9");var subQ3=sQuery(id+"F0.wireOp",EDGE,"E6.right");var subQ6=makeQuery(id+"F0.imprint","INTERSECT",VERTEX,{"derivedFrom":[subQ3,subQ0]});Q7=makeQuery(id+"F9.boolean.opBoolean","SPLIT",FACE,{"disambiguationData":[TD([makeQuery(id+"F9.opExtrude","SWEPT_FACE",FACE,{"disambiguationData":[OSD([sQuery(id+"F8.wireOp",EDGE,"E23.left")])]})])],"derivedFrom":makeQuery(id+"F5.opExtrude","SWEPT_FACE",FACE,{"disambiguationData":[OSD([subQ0]),TDD([makeQuery(id+"F0.imprint","IMPRINT",EDGE,{"disambiguationData":[TD([[subQ6,-1.0]])],"derivedFrom":subQ0})])]})});}
            extrude(context, id + "F10", {"entities" : qUnion([Q0, Q1, Q2, Q3, Q4, Q5, Q6, Q7]), "operationType" : NewBodyOperationType.REMOVE, "oppositeDirection" : true, "depth" : 50 * mm});
        }
        {
            var Q0;
            Q0=makeQuery(id+"F1.opExtrude","SWEPT_FACE",FACE,{"disambiguationData":[OSD([sQuery(id+"F0.wireOp",EDGE,"E1.left")])]});
            var sketch = newSketch(context, id + "F11", { "sketchPlane" : qUnion([Q0])});
            skLineSegment(sketch, "E25.bottom", {"start": v(-1662, 25.5) * mm, "end": v(-1750, 25.5) * mm});
            skLineSegment(sketch, "E25.top", {"start": v(-1662, -25.5) * mm, "end": v(-1750, -25.5) * mm});
            skLineSegment(sketch, "E25.left", {"start": v(-1662, 25.5) * mm, "end": v(-1662, -25.5) * mm});
            skLineSegment(sketch, "E25.right", {"start": v(-1750, 25.5) * mm, "end": v(-1750, -25.5) * mm});
            skPoint(sketch, "E25.middle", {"position": v(-1706, 0) * mm});
            skPoint(sketch, "E25.middle.positionSnap0", {"position": v(-1800, 0) * mm});
            skPoint(sketch, "E25.centerSnap0", {"position": v(-1800, 0) * mm});
            skPoint(sketch, "E26.endSnap0", {"position": v(-1706, -25.5) * mm});
            skLineSegment(sketch, "E27.bottom", {"start": v(-1739, -63.5) * mm, "end": v(-1673, -63.5) * mm});
            skLineSegment(sketch, "E27.top", {"start": v(-1739, 63.5) * mm, "end": v(-1673, 63.5) * mm});
            skLineSegment(sketch, "E27.left", {"start": v(-1744, -58.5) * mm, "end": v(-1744, 58.5) * mm});
            skLineSegment(sketch, "E27.right", {"start": v(-1668, -58.5) * mm, "end": v(-1668, 58.5) * mm});
            skPoint(sketch, "E28.visualSharp", {"position": v(-1744, -63.5) * mm});
            skArc(sketch, "E28.filletArc", {"start": v(-1744, -58.5) * mm, "mid": v(-1742.54, -62.04) * mm, "end": v(-1739, -63.5) * mm});
            skPoint(sketch, "E29.visualSharp", {"position": v(-1668, -63.5) * mm});
            skArc(sketch, "E29.filletArc", {"start": v(-1673, -63.5) * mm, "mid": v(-1669.46, -62.04) * mm, "end": v(-1668, -58.5) * mm});
            skPoint(sketch, "E30.visualSharp", {"position": v(-1668, 63.5) * mm});
            skArc(sketch, "E30.filletArc", {"start": v(-1668, 58.5) * mm, "mid": v(-1669.46, 62.04) * mm, "end": v(-1673, 63.5) * mm});
            skPoint(sketch, "E31.visualSharp", {"position": v(-1744, 63.5) * mm});
            skArc(sketch, "E31.filletArc", {"start": v(-1739, 63.5) * mm, "mid": v(-1742.54, 62.04) * mm, "end": v(-1744, 58.5) * mm});
            skSolve(sketch);
        }
        {
            var Q0;
            Q0=makeQuery(id+"F11.imprint","IMPRINT",FACE,{"disambiguationData":[TD([[makeQuery(id+"F11.imprint","IMPRINT",EDGE,{"derivedFrom":sQuery(id+"F11.wireOp",EDGE,"E27.bottom")}),1.0]])]});
            var Q1;
            Q1=makeQuery(id+"F11.imprint","IMPRINT",FACE,{"disambiguationData":[TD([[makeQuery(id+"F11.imprint","IMPRINT",EDGE,{"derivedFrom":sQuery(id+"F11.wireOp",EDGE,"E27.top")}),-1.0]])]});
            extrude(context, id + "F12", {"entities" : qUnion([Q0, Q1]), "operationType" : NewBodyOperationType.ADD, "oppositeDirection" : true, "depth" : 6000 * mm});
        }
    });
